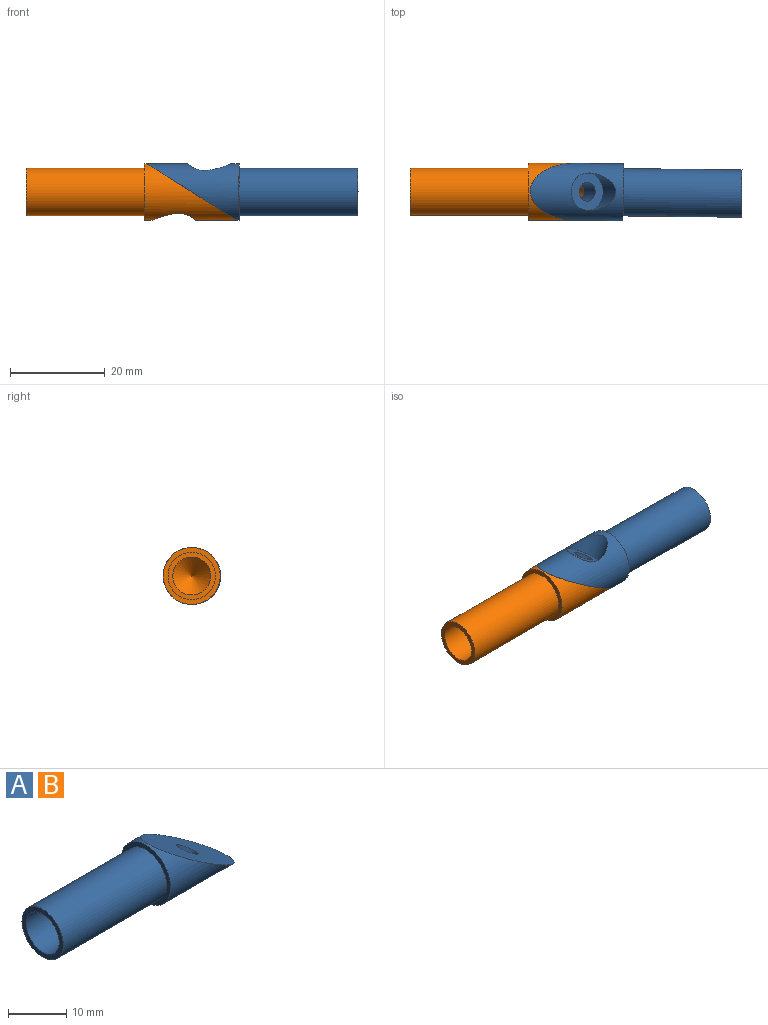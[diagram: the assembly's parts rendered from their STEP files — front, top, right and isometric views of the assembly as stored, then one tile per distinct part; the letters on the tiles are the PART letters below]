
ASSEMBLY  parts=2 mates=1
PART A: 10 faces, bbox 44.7x12x16.2 mm
  f0: plane 10x10mm, normal (-1,0,0), area 28.3mm2, adj f3,f8
  f1: cylinder r=6mm len=19.73mm, axis (-1,0,0), area 315.5mm2, adj f2,f4,f7
  f2: plane 12x12mm, normal (-1,0,0), area 34.6mm2, adj f1,f3
  f3: cylinder r=5mm len=25mm, axis (-1,0,0), area 785.4mm2, adj f0,f2
  f4: plane 19.2x12mm, normal (0.53,0,0.85), area 200.9mm2, adj f1,f5
  f5: cylinder r=2mm len=5.94mm, axis (0.53,0,0.85), area 56.5mm2, adj f4,f6
  f6: plane 7.9x6.7mm, normal (-0.53,0,-0.85), area 36.5mm2, adj f5,f7
  f7: cylinder r=3.95mm len=9.37mm, axis (0.53,0,0.85), area 42.9mm2, adj f1,f6
  f8: cylinder r=4mm len=22mm, axis (-1,0,0), area 552.9mm2, adj f0,f9
  f9: cone r=4mm half-angle=45deg, axis (-1,0,0), area 71.1mm2, adj f8
PART B: same geometry as A
PLACE A rot(axis=(0.01,1,0),180deg) t=(51.03,4.34,-1.61)mm
PLACE B rot(axis=(0,1,0),0deg) t=(-18.97,4.74,-1.62)mm fixed
MATE revolute B.f5 <-> A.f5  axis (0.53,0,0.85) through (16.03,4.74,-1.62)mm
